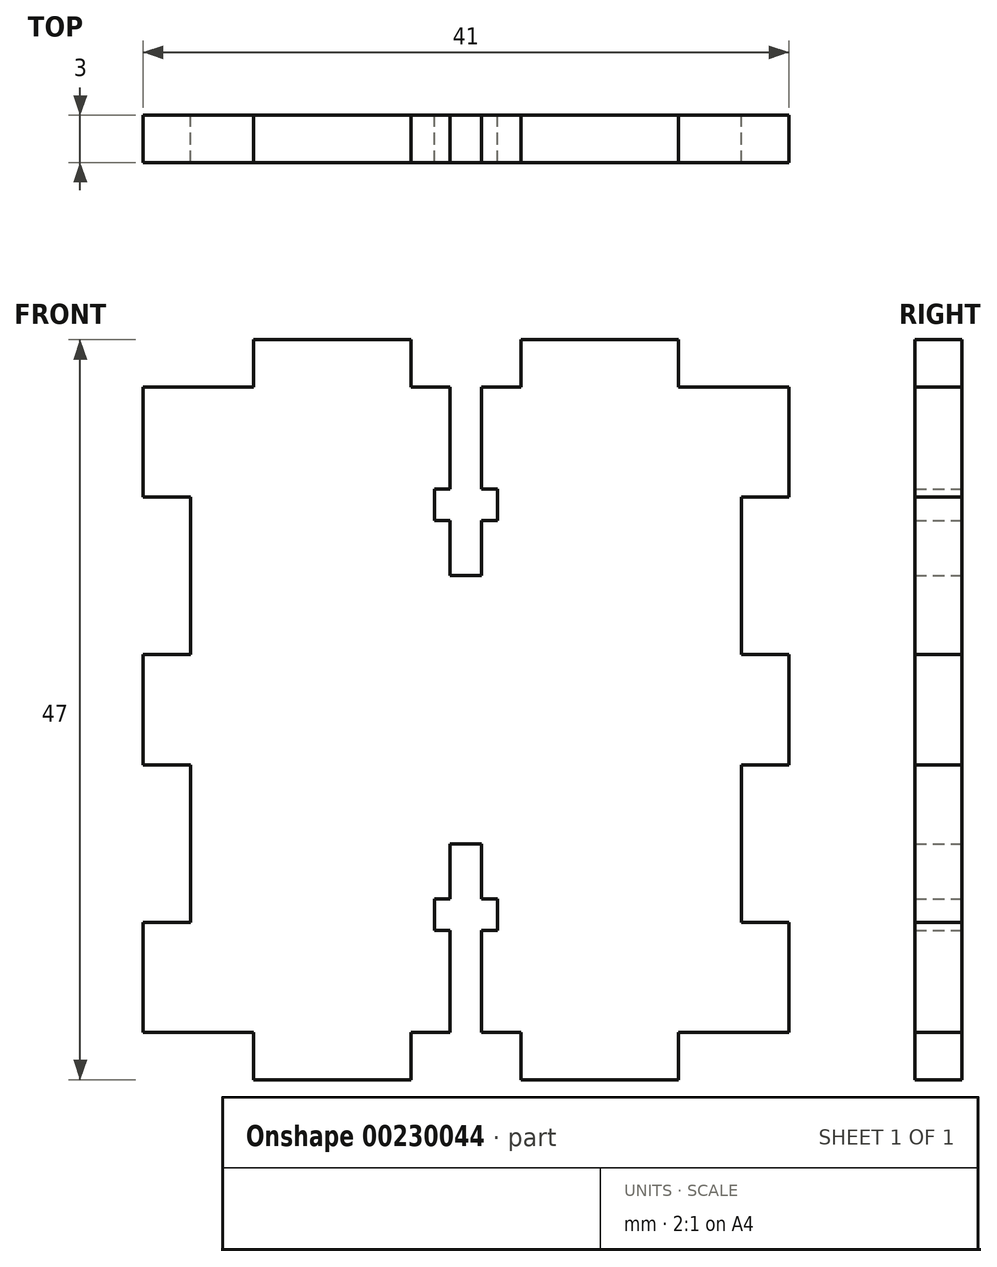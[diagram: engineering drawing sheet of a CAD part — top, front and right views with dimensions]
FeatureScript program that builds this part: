
annotation { "Feature Type Name" : "Feature", "Feature Type Description" : "" }
export const myFeature = defineFeature(function(context is Context, id is Id, definition is map)
    precondition{}
    {
        {
            var Q0;
            Q0=qCreatedBy(makeId("Front.planeOp"),FACE);
            var sketch = newSketch(context, id + "F0", { "sketchPlane" : qUnion([Q0])});
            skLineSegment(sketch, "E0", {"start": v(7.55, 0) * mm, "end": v(7.55, 7) * mm});
            skLineSegment(sketch, "E1", {"start": v(7.55, 7) * mm, "end": v(10.55, 7) * mm});
            skLineSegment(sketch, "E2", {"start": v(10.55, 7) * mm, "end": v(10.55, 17) * mm});
            skLineSegment(sketch, "E3", {"start": v(10.55, 17) * mm, "end": v(7.55, 17) * mm});
            skLineSegment(sketch, "E4", {"start": v(7.55, 17) * mm, "end": v(7.55, 24) * mm});
            skLineSegment(sketch, "E5", {"start": v(7.55, 24) * mm, "end": v(10.55, 24) * mm});
            skLineSegment(sketch, "E6", {"start": v(10.55, 24) * mm, "end": v(10.55, 34) * mm});
            skLineSegment(sketch, "E7", {"start": v(10.55, 34) * mm, "end": v(7.55, 34) * mm});
            skLineSegment(sketch, "E8", {"start": v(7.55, 34) * mm, "end": v(7.55, 41) * mm});
            skLineSegment(sketch, "E9", {"start": v(7.55, 41) * mm, "end": v(14.55, 41) * mm});
            skLineSegment(sketch, "E10", {"start": v(14.55, 41) * mm, "end": v(14.55, 44) * mm});
            skLineSegment(sketch, "E11", {"start": v(14.55, 44) * mm, "end": v(24.55, 44) * mm});
            skLineSegment(sketch, "E12", {"start": v(24.55, 44) * mm, "end": v(24.55, 41) * mm});
            skLineSegment(sketch, "E13", {"start": v(24.55, 41) * mm, "end": v(27.04, 41) * mm});
            skLineSegment(sketch, "E14", {"start": v(28.05, 29.01) * mm, "end": v(28.05, 0) * mm, "construction": true});
            skLineSegment(sketch, "E15", {"start": v(7.55, 20.5) * mm, "end": v(28.05, 20.5) * mm, "construction": true});
            skLineSegment(sketch, "E16.MirrorCS", {"start": v(48.55, 7) * mm, "end": v(45.55, 7) * mm});
            skLineSegment(sketch, "E17.MirrorCS", {"start": v(31.55, 44) * mm, "end": v(31.55, 41) * mm});
            skLineSegment(sketch, "E18.MirrorCS", {"start": v(41.55, 41) * mm, "end": v(41.55, 44) * mm});
            skLineSegment(sketch, "E19.MirrorCS", {"start": v(45.55, 17) * mm, "end": v(48.55, 17) * mm});
            skLineSegment(sketch, "E20.MirrorCS", {"start": v(48.55, 24) * mm, "end": v(45.55, 24) * mm});
            skLineSegment(sketch, "E21.MirrorCS", {"start": v(45.55, 34) * mm, "end": v(48.55, 34) * mm});
            skLineSegment(sketch, "E22.MirrorCS", {"start": v(31.55, 41) * mm, "end": v(29.04, 41) * mm});
            skLineSegment(sketch, "E23.MirrorCS", {"start": v(45.55, 7) * mm, "end": v(45.55, 17) * mm});
            skLineSegment(sketch, "E24.MirrorCS", {"start": v(48.55, 17) * mm, "end": v(48.55, 24) * mm});
            skLineSegment(sketch, "E25.MirrorCS", {"start": v(48.55, 20.5) * mm, "end": v(28.05, 20.5) * mm, "construction": true});
            skLineSegment(sketch, "E26.MirrorCS", {"start": v(48.55, 0) * mm, "end": v(48.55, 7) * mm});
            skLineSegment(sketch, "E27.MirrorCS", {"start": v(41.55, 44) * mm, "end": v(31.55, 44) * mm});
            skLineSegment(sketch, "E28.MirrorCS", {"start": v(48.55, 41) * mm, "end": v(41.55, 41) * mm});
            skLineSegment(sketch, "E29.MirrorCS", {"start": v(45.55, 24) * mm, "end": v(45.55, 34) * mm});
            skLineSegment(sketch, "E30.MirrorCS", {"start": v(48.55, 34) * mm, "end": v(48.55, 41) * mm});
            skLineSegment(sketch, "E31.MirrorCS", {"start": v(30.04, 34.51) * mm, "end": v(29.04, 34.51) * mm});
            skLineSegment(sketch, "E32.MirrorCS", {"start": v(30.04, 34.51) * mm, "end": v(30.04, 32.51) * mm});
            skLineSegment(sketch, "E33.MirrorCS", {"start": v(30.04, 32.51) * mm, "end": v(29.04, 32.51) * mm});
            skLineSegment(sketch, "E34.MirrorCS", {"start": v(27.04, 32.51) * mm, "end": v(26.04, 32.51) * mm});
            skLineSegment(sketch, "E35.MirrorCS", {"start": v(29.04, 29.01) * mm, "end": v(27.04, 29.01) * mm});
            skLineSegment(sketch, "E36.MirrorCS", {"start": v(26.04, 34.51) * mm, "end": v(26.04, 32.51) * mm});
            skLineSegment(sketch, "E37.MirrorCS", {"start": v(27.04, 34.51) * mm, "end": v(26.04, 34.51) * mm});
            skLineSegment(sketch, "E38.MirrorCS", {"start": v(29.04, 41.01) * mm, "end": v(29.04, 34.51) * mm});
            skLineSegment(sketch, "E39.MirrorCS", {"start": v(27.04, 41.01) * mm, "end": v(27.04, 34.51) * mm});
            skLineSegment(sketch, "E40.MirrorCS", {"start": v(29.04, 32.51) * mm, "end": v(29.04, 29.01) * mm});
            skLineSegment(sketch, "E41.MirrorCS", {"start": v(27.04, 32.51) * mm, "end": v(27.04, 29.01) * mm});
            skPoint(sketch, "E42.orphan", {"position": v(28.05, 41) * mm});
            skLineSegment(sketch, "E43.MirrorCS", {"start": v(26.04, 6.49) * mm, "end": v(26.04, 8.49) * mm});
            skLineSegment(sketch, "E44.MirrorCS", {"start": v(27.04, 6.49) * mm, "end": v(26.04, 6.49) * mm});
            skLineSegment(sketch, "E45.MirrorCS", {"start": v(30.04, 8.49) * mm, "end": v(29.04, 8.49) * mm});
            skLineSegment(sketch, "E46.MirrorCS", {"start": v(27.04, 8.49) * mm, "end": v(26.04, 8.49) * mm});
            skLineSegment(sketch, "E47.MirrorCS", {"start": v(29.04, 11.99) * mm, "end": v(27.04, 11.99) * mm});
            skLineSegment(sketch, "E48.MirrorCS", {"start": v(24.55, -3) * mm, "end": v(24.55, 0) * mm});
            skLineSegment(sketch, "E49.MirrorCS", {"start": v(41.55, 0) * mm, "end": v(41.55, -3) * mm});
            skLineSegment(sketch, "E50.MirrorCS", {"start": v(30.04, 6.49) * mm, "end": v(29.04, 6.49) * mm});
            skLineSegment(sketch, "E51.MirrorCS", {"start": v(27.04, 8.49) * mm, "end": v(27.04, 11.99) * mm});
            skLineSegment(sketch, "E52.MirrorCS", {"start": v(14.55, 0) * mm, "end": v(14.55, -3) * mm});
            skLineSegment(sketch, "E53.MirrorCS", {"start": v(31.55, -3) * mm, "end": v(31.55, 0) * mm});
            skLineSegment(sketch, "E54.MirrorCS", {"start": v(24.55, 0) * mm, "end": v(27.04, 0) * mm});
            skLineSegment(sketch, "E55.MirrorCS", {"start": v(31.55, 0) * mm, "end": v(29.04, 0) * mm});
            skLineSegment(sketch, "E56.MirrorCS", {"start": v(30.04, 6.49) * mm, "end": v(30.04, 8.49) * mm});
            skLineSegment(sketch, "E57.MirrorCS", {"start": v(29.04, 8.49) * mm, "end": v(29.04, 11.99) * mm});
            skLineSegment(sketch, "E58.MirrorCS", {"start": v(7.55, 17) * mm, "end": v(10.55, 17) * mm});
            skLineSegment(sketch, "E59.MirrorCS", {"start": v(45.55, 7) * mm, "end": v(48.55, 7) * mm});
            skLineSegment(sketch, "E60.MirrorCS", {"start": v(48.55, 17) * mm, "end": v(45.55, 17) * mm});
            skLineSegment(sketch, "E61.MirrorCS", {"start": v(10.55, 7) * mm, "end": v(7.55, 7) * mm});
            skPoint(sketch, "E62.MirrorP", {"position": v(28.05, 0) * mm});
            skLineSegment(sketch, "E63.MirrorCS", {"start": v(10.55, 17) * mm, "end": v(10.55, 7) * mm});
            skLineSegment(sketch, "E64.MirrorCS", {"start": v(29.04, -0.01) * mm, "end": v(29.04, 6.49) * mm});
            skLineSegment(sketch, "E65.MirrorCS", {"start": v(7.55, 0) * mm, "end": v(14.55, 0) * mm});
            skLineSegment(sketch, "E66.MirrorCS", {"start": v(48.55, 0) * mm, "end": v(41.55, 0) * mm});
            skLineSegment(sketch, "E67.MirrorCS", {"start": v(7.55, 7) * mm, "end": v(7.55, 0) * mm});
            skLineSegment(sketch, "E68.MirrorCS", {"start": v(14.55, -3) * mm, "end": v(24.55, -3) * mm});
            skLineSegment(sketch, "E69.MirrorCS", {"start": v(45.55, 17) * mm, "end": v(45.55, 7) * mm});
            skLineSegment(sketch, "E70.MirrorCS", {"start": v(27.04, -0.01) * mm, "end": v(27.04, 6.49) * mm});
            skLineSegment(sketch, "E71.MirrorCS", {"start": v(41.55, -3) * mm, "end": v(31.55, -3) * mm});
            skLineSegment(sketch, "E72.MirrorCS", {"start": v(48.55, 7) * mm, "end": v(48.55, 0) * mm});
            skSolve(sketch);
        }
        {
            var Q0;
            Q0=makeQuery(id+"F0.imprint","IMPRINT",FACE,{"disambiguationData":[TD([[makeQuery(id+"F0.imprint","IMPRINT",EDGE,{"derivedFrom":sQuery(id+"F0.wireOp",EDGE,"E4")}),-1.0]])]});
            extrude(context, id + "F1", {"entities" : qUnion([Q0]), "depth" : 3 * mm});
        }
    });
